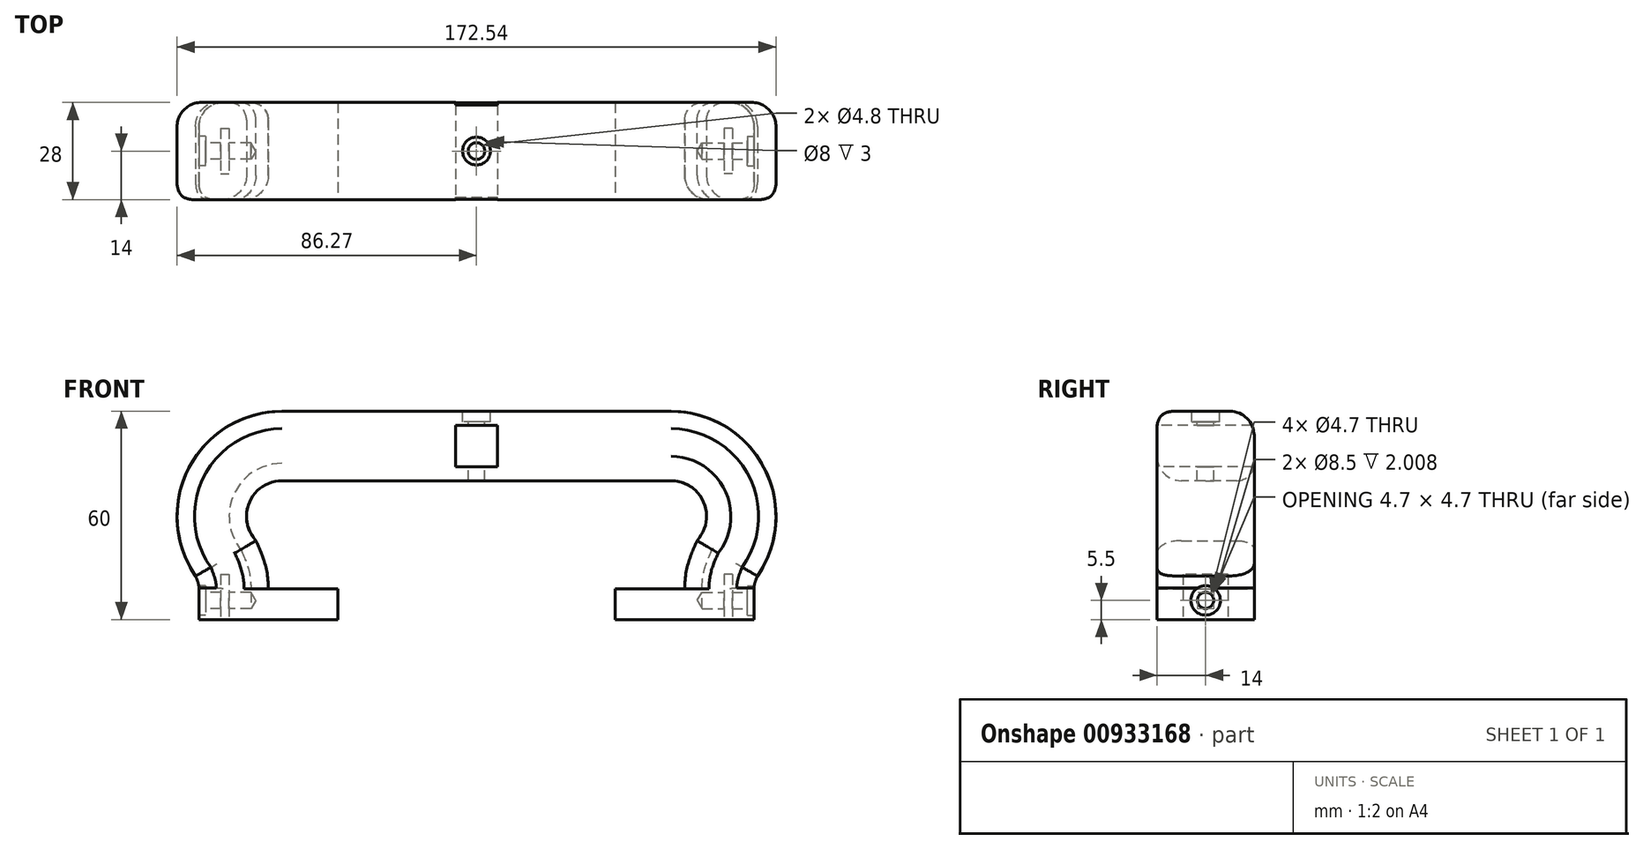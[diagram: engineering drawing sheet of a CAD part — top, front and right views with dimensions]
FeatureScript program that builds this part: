
annotation { "Feature Type Name" : "Feature", "Feature Type Description" : "" }
export const myFeature = defineFeature(function(context is Context, id is Id, definition is map)
    precondition{}
    {
        {
            var Q0;
            Q0=qCreatedBy(makeId("Right.planeOp"),FACE);
            var sketch = newSketch(context, id + "F0", { "sketchPlane" : qUnion([Q0])});
            skLineSegment(sketch, "E0.bottom", {"start": v(14, 60) * mm, "end": v(-14, 60) * mm});
            skLineSegment(sketch, "E0.top", {"start": v(14, 40) * mm, "end": v(-14, 40) * mm});
            skLineSegment(sketch, "E0.left", {"start": v(14, 40) * mm, "end": v(14, 60) * mm});
            skLineSegment(sketch, "E0.right", {"start": v(-14, 40) * mm, "end": v(-14, 60) * mm});
            skPoint(sketch, "E0.middle", {"position": v(0, 50) * mm});
            skSolve(sketch);
        }
        {
            var Q0;
            Q0=qCreatedBy(makeId("Front.planeOp"),FACE);
            var sketch = newSketch(context, id + "F1", { "sketchPlane" : qUnion([Q0])});
            skPoint(sketch, "E1.0", {"position": v(0, 50) * mm});
            skPoint(sketch, "E2", {"position": v(70, 0) * mm});
            skLineSegment(sketch, "E3", {"start": v(0, 50) * mm, "end": v(56.02, 50) * mm});
            skLineSegment(sketch, "E4", {"start": v(70, 0) * mm, "end": v(70, 8.96) * mm});
            skPoint(sketch, "E5", {"position": v(72.2, 17.57) * mm});
            skFitSpline(sketch, "E6", {"points": [v(72.2, 17.57) * mm, v(70, 8.96) * mm], "startDerivative": vector(-4.3, -9.4) * mm, "endDerivative": vector(0.3, -8.61) * mm});
            skArc(sketch, "E7", {"start": v(56.02, 50) * mm, "mid": v(74.14, 38.79) * mm, "end": v(72.2, 17.57) * mm});
            skSolve(sketch);
        }
        {
            var Q0;
            Q0=makeQuery(id+"F0.imprint","IMPRINT",FACE,{"disambiguationData":[TD([[makeQuery(id+"F0.imprint","IMPRINT",EDGE,{"derivedFrom":sQuery(id+"F0.wireOp",EDGE,"E0.bottom")}),1.0]])]});
            var Q1;
            Q1=sQuery(id+"F1.wireOp",EDGE,"E3");
            var Q2;
            Q2=sQuery(id+"F1.wireOp",EDGE,"E7");
            var Q3;
            Q3=sQuery(id+"F1.wireOp",EDGE,"E6");
            var Q4;
            Q4=sQuery(id+"F1.wireOp",EDGE,"E4");
            sweep(context, id + "F2", {"profiles" : qUnion([Q0]), "path" : qUnion([Q1, Q2, Q3, Q4])});
        }
        {
            var Q0;
            Q0=makeQuery(id+"F2.opSweep","SWEPT_BODY",BODY,{"disambiguationData":[OSD([sQuery(id+"F0.wireOp",EDGE,"E0.bottom"),sQuery(id+"F0.wireOp",EDGE,"E0.top"),sQuery(id+"F0.wireOp",EDGE,"E0.left"),sQuery(id+"F0.wireOp",EDGE,"E0.right"),sQuery(id+"F1.wireOp",EDGE,"E4")])]});
            var Q1;
            Q1=qCreatedBy(makeId("Right.planeOp"),FACE);
            mirror(context, id + "F3", {"operationType" : NewBodyOperationType.ADD, "entities" : qUnion([Q0]), "mirrorPlane" : qUnion([Q1])});
        }
        {
            var Q0;
            {var subQ0=makeQuery(id+"F2.opSweep","SWEPT_FACE",FACE,{"disambiguationData":[OSD([sQuery(id+"F0.wireOp",EDGE,"E0.right"),sQuery(id+"F1.wireOp",EDGE,"E3")])]});Q0=makeQuery(id+"F3.boolean.opBoolean","MERGE",FACE,{"derivedFrom":[subQ0,makeQuery(id+"F3.opPattern","COPY",FACE,{"derivedFrom":subQ0,"instanceName":"1"})]});}
            var sketch = newSketch(context, id + "F4", { "sketchPlane" : qUnion([Q0])});
            skLineSegment(sketch, "E8.0", {"start": v(0, 40) * mm, "end": v(0, 60) * mm});
            skPoint(sketch, "E9", {"position": v(0, 50) * mm});
            skLineSegment(sketch, "E10.bottom", {"start": v(6, 44) * mm, "end": v(-6, 44) * mm});
            skLineSegment(sketch, "E10.top", {"start": v(6, 56) * mm, "end": v(-6, 56) * mm});
            skLineSegment(sketch, "E10.left", {"start": v(6, 44) * mm, "end": v(6, 56) * mm});
            skLineSegment(sketch, "E10.right", {"start": v(-6, 44) * mm, "end": v(-6, 56) * mm});
            skSolve(sketch);
        }
        {
            var Q0;
            {var subQ5=sQuery(id+"F4.wireOp",EDGE,"E10.right");Q0=makeQuery(id+"F4.imprint","IMPRINT",FACE,{"disambiguationData":[TD([[makeQuery(id+"F4.imprint","IMPRINT",EDGE,{"derivedFrom":subQ5}),-1.0]])]});}
            var Q1;
            {var subQ5=sQuery(id+"F4.wireOp",EDGE,"E10.left");Q1=makeQuery(id+"F4.imprint","IMPRINT",FACE,{"disambiguationData":[TD([[makeQuery(id+"F4.imprint","IMPRINT",EDGE,{"derivedFrom":subQ5}),1.0]])]});}
            extrude(context, id + "F5", {"entities" : qUnion([Q0, Q1]), "operationType" : NewBodyOperationType.REMOVE, "endBound" : BoundingType.THROUGH_ALL, "oppositeDirection" : true, "depth" : 18 * mm, "offsetDistance" : 25 * mm});
        }
        {
            var Q0;
            Q0=makeQuery(id+"F2.opSweep","CAP_FACE",FACE,{"disambiguationData":[OSD([sQuery(id+"F0.wireOp",EDGE,"E0.bottom"),sQuery(id+"F0.wireOp",EDGE,"E0.top"),sQuery(id+"F0.wireOp",EDGE,"E0.left"),sQuery(id+"F0.wireOp",EDGE,"E0.right"),sQuery(id+"F1.wireOp",VERTEX,"E4.start")])],"isStart":false});
            var sketch = newSketch(context, id + "F6", { "sketchPlane" : qUnion([Q0])});
            skLineSegment(sketch, "E11.0", {"start": v(0, -14) * mm, "end": v(0, 14) * mm, "construction": true});
            skLineSegment(sketch, "E12", {"start": v(72.5, 14) * mm, "end": v(72.5, -14) * mm, "construction": true});
            skLineSegment(sketch, "E13.MirrorCS", {"start": v(-72.5, 14) * mm, "end": v(-72.5, -14) * mm, "construction": true});
            skPoint(sketch, "E14", {"position": v(72.5, 0) * mm});
            skLineSegment(sketch, "E15.bottom", {"start": v(73.7, -6.5) * mm, "end": v(71.3, -6.5) * mm});
            skLineSegment(sketch, "E15.top", {"start": v(73.7, 6.5) * mm, "end": v(71.3, 6.5) * mm});
            skLineSegment(sketch, "E15.left", {"start": v(73.7, -6.5) * mm, "end": v(73.7, 6.5) * mm});
            skLineSegment(sketch, "E15.right", {"start": v(71.3, -6.5) * mm, "end": v(71.3, 6.5) * mm});
            skLineSegment(sketch, "E16.MirrorCS", {"start": v(-71.3, -6.5) * mm, "end": v(-71.3, 6.5) * mm});
            skLineSegment(sketch, "E17.MirrorCS", {"start": v(-73.7, -6.5) * mm, "end": v(-73.7, 6.5) * mm});
            skLineSegment(sketch, "E18.MirrorCS", {"start": v(-73.7, 6.5) * mm, "end": v(-71.3, 6.5) * mm});
            skLineSegment(sketch, "E19.MirrorCS", {"start": v(-73.7, -6.5) * mm, "end": v(-71.3, -6.5) * mm});
            skSolve(sketch);
        }
        {
            var Q0;
            Q0=makeQuery(id+"F6.imprint","IMPRINT",FACE,{"disambiguationData":[TD([[makeQuery(id+"F6.imprint","IMPRINT",EDGE,{"derivedFrom":sQuery(id+"F6.wireOp",EDGE,"E15.bottom")}),-1.0]])]});
            var Q1;
            Q1=makeQuery(id+"F6.imprint","IMPRINT",FACE,{"disambiguationData":[TD([[makeQuery(id+"F6.imprint","IMPRINT",EDGE,{"derivedFrom":sQuery(id+"F6.wireOp",EDGE,"E16.MirrorCS")}),1.0]])]});
            extrude(context, id + "F7", {"entities" : qUnion([Q0, Q1]), "operationType" : NewBodyOperationType.REMOVE, "oppositeDirection" : true, "depth" : 13 * mm, "offsetDistance" : 25 * mm});
        }
        {
            var Q0;
            Q0=makeQuery(id+"F2.opSweep","SWEPT_FACE",FACE,{"disambiguationData":[OSD([sQuery(id+"F0.wireOp",EDGE,"E0.bottom"),sQuery(id+"F1.wireOp",EDGE,"E4")])]});
            var sketch = newSketch(context, id + "F8", { "sketchPlane" : qUnion([Q0])});
            skPoint(sketch, "E20", {"position": v(0, 5.5) * mm});
            skPoint(sketch, "E20.positionSnap0", {"position": v(0, 9.13) * mm});
            skSolve(sketch);
        }
        {
            var Q0;
            Q0=makeQuery(id+"F2.opSweep","SWEPT_FACE",FACE,{"disambiguationData":[OSD([sQuery(id+"F0.wireOp",EDGE,"E0.top"),sQuery(id+"F1.wireOp",EDGE,"E4")])]});
            extrude(context, id + "F9", {"entities" : qUnion([Q0]), "operationType" : NewBodyOperationType.ADD, "depth" : 20 * mm, "offsetDistance" : 25 * mm});
        }
        {
            var Q0;
            Q0=makeQuery(id+"F3.opPattern","COPY",FACE,{"derivedFrom":makeQuery(id+"F2.opSweep","SWEPT_FACE",FACE,{"disambiguationData":[OSD([sQuery(id+"F0.wireOp",EDGE,"E0.bottom"),sQuery(id+"F1.wireOp",EDGE,"E4")])]}),"instanceName":"1"});
            var sketch = newSketch(context, id + "F10", { "sketchPlane" : qUnion([Q0])});
            skPoint(sketch, "E21", {"position": v(0, 5.5) * mm});
            skPoint(sketch, "E21.positionSnap0", {"position": v(0, 9.13) * mm});
            skSolve(sketch);
        }
        {
            var Q0;
            Q0=makeQuery(id+"F3.opPattern","COPY",FACE,{"derivedFrom":makeQuery(id+"F2.opSweep","SWEPT_FACE",FACE,{"disambiguationData":[OSD([sQuery(id+"F0.wireOp",EDGE,"E0.top"),sQuery(id+"F1.wireOp",EDGE,"E4")])]}),"instanceName":"1"});
            extrude(context, id + "F11", {"entities" : qUnion([Q0]), "operationType" : NewBodyOperationType.ADD, "depth" : 20 * mm, "offsetDistance" : 25 * mm});
        }
        {
            var Q0;
            {var subQ0=makeQuery(id+"F2.opSweep","SWEPT_FACE",FACE,{"disambiguationData":[OSD([sQuery(id+"F0.wireOp",EDGE,"E0.bottom"),sQuery(id+"F1.wireOp",EDGE,"E3")])]});Q0=makeQuery(id+"F3.boolean.opBoolean","MERGE",FACE,{"derivedFrom":[subQ0,makeQuery(id+"F3.opPattern","COPY",FACE,{"derivedFrom":subQ0,"instanceName":"1"})]});}
            var sketch = newSketch(context, id + "F12", { "sketchPlane" : qUnion([Q0])});
            skPoint(sketch, "E22", {"position": v(0, 0) * mm});
            skSolve(sketch);
        }
        {
            var Q0;
            Q0=sQuery(id+"F12.wireOp",VERTEX,"E22");
            var Q1;
            Q1=makeQuery(id+"F2.opSweep","SWEPT_BODY",BODY,{"disambiguationData":[OSD([sQuery(id+"F0.wireOp",EDGE,"E0.bottom"),sQuery(id+"F0.wireOp",EDGE,"E0.top"),sQuery(id+"F0.wireOp",EDGE,"E0.left"),sQuery(id+"F0.wireOp",EDGE,"E0.right"),sQuery(id+"F1.wireOp",EDGE,"E4")])]});
            hole(context, id + "F13", {"style" : HoleStyle.C_BORE, "endStyle" : HoleEndStyle.THROUGH, "holeDiameter" : 4.8 * mm, "cBoreDiameter" : 8 * mm, "cBoreDepth" : 3 * mm, "majorDiameter" : 5 * mm, "isTappedThrough" : true, "tappedDepth" : 12 * mm, "tapClearance" : 3, "locations" : qUnion([Q0]), "scope" : qUnion([Q1])});
        }
        {
            var Q0;
            {var subQ0=makeQuery(id+"F2.opSweep","SWEPT_EDGE",EDGE,{"disambiguationData":[OSD([sQuery(id+"F0.wireOp",EDGE,"E0.bottom"),sQuery(id+"F0.wireOp",EDGE,"E0.right"),sQuery(id+"F1.wireOp",EDGE,"E3")])]});Q0=makeQuery(id+"F3.boolean.opBoolean","MERGE",EDGE,{"derivedFrom":[subQ0,makeQuery(id+"F3.opPattern","COPY",EDGE,{"derivedFrom":subQ0,"instanceName":"1"})]});}
            var Q1;
            Q1=makeQuery(id+"F2.opSweep","SWEPT_EDGE",EDGE,{"disambiguationData":[OSD([sQuery(id+"F0.wireOp",EDGE,"E0.bottom"),sQuery(id+"F0.wireOp",EDGE,"E0.right"),sQuery(id+"F1.wireOp",EDGE,"E7")])]});
            var Q2;
            Q2=makeQuery(id+"F2.opSweep","SWEPT_EDGE",EDGE,{"disambiguationData":[OSD([sQuery(id+"F0.wireOp",EDGE,"E0.bottom"),sQuery(id+"F0.wireOp",EDGE,"E0.right"),sQuery(id+"F1.wireOp",EDGE,"E6")]),OD(1.0)]});
            var Q3;
            {var subQ0=sQuery(id+"F19.hole-0.sketch.wireOp",EDGE,"cbore_start_line_2");Q3=makeQuery(id+"F19.hole-0.boolean.opBoolean","COPY",EDGE,{"disambiguationData":[topologyDisambiguationEdgeConnected([makeQuery(id+"F2.opSweep","SWEPT_FACE",FACE,{"disambiguationData":[OSD([sQuery(id+"F0.wireOp",EDGE,"E0.bottom"),sQuery(id+"F1.wireOp",EDGE,"E4")])]}),makeQuery(id+"F19.hole-0.opRevolve","SWEPT_FACE",FACE,{"disambiguationData":[OSD([subQ0])]})])],"derivedFrom":makeQuery(id+"F19.hole-0.opRevolve","SWEPT_EDGE",EDGE,{"disambiguationData":[OSD([subQ0,sQuery(id+"F19.hole-0.sketch.wireOp",EDGE,"cbore_start_line_3")])]})});}
            var Q4;
            Q4=makeQuery(id+"F2.opSweep","SWEPT_EDGE",EDGE,{"disambiguationData":[OSD([sQuery(id+"F0.wireOp",EDGE,"E0.bottom"),sQuery(id+"F0.wireOp",EDGE,"E0.right"),sQuery(id+"F1.wireOp",EDGE,"E4")])]});
            var Q5;
            Q5=makeQuery(id+"F3.opPattern","COPY",EDGE,{"derivedFrom":makeQuery(id+"F2.opSweep","SWEPT_EDGE",EDGE,{"disambiguationData":[OSD([sQuery(id+"F0.wireOp",EDGE,"E0.bottom"),sQuery(id+"F0.wireOp",EDGE,"E0.right"),sQuery(id+"F1.wireOp",EDGE,"E7")])]}),"instanceName":"1"});
            var Q6;
            Q6=makeQuery(id+"F3.opPattern","COPY",EDGE,{"derivedFrom":makeQuery(id+"F2.opSweep","SWEPT_EDGE",EDGE,{"disambiguationData":[OSD([sQuery(id+"F0.wireOp",EDGE,"E0.bottom"),sQuery(id+"F0.wireOp",EDGE,"E0.right"),sQuery(id+"F1.wireOp",EDGE,"E6")]),OD(1.0)]}),"instanceName":"1"});
            var Q7;
            Q7=makeQuery(id+"F3.opPattern","COPY",EDGE,{"derivedFrom":makeQuery(id+"F2.opSweep","SWEPT_EDGE",EDGE,{"disambiguationData":[OSD([sQuery(id+"F0.wireOp",EDGE,"E0.bottom"),sQuery(id+"F0.wireOp",EDGE,"E0.right"),sQuery(id+"F1.wireOp",EDGE,"E4")])]}),"instanceName":"1"});
            var Q8;
            Q8=makeQuery(id+"F2.opSweep","SWEPT_EDGE",EDGE,{"disambiguationData":[OSD([sQuery(id+"F0.wireOp",EDGE,"E0.bottom"),sQuery(id+"F0.wireOp",EDGE,"E0.right"),sQuery(id+"F1.wireOp",EDGE,"E6")]),OD(0.0)]});
            var Q9;
            Q9=makeQuery(id+"F3.opPattern","COPY",EDGE,{"derivedFrom":makeQuery(id+"F2.opSweep","SWEPT_EDGE",EDGE,{"disambiguationData":[OSD([sQuery(id+"F0.wireOp",EDGE,"E0.bottom"),sQuery(id+"F0.wireOp",EDGE,"E0.right"),sQuery(id+"F1.wireOp",EDGE,"E6")]),OD(0.0)]}),"instanceName":"1"});
            fillet(context, id + "F14", {"entities" : qUnion([Q0, Q1, Q2, Q3, Q4, Q5, Q6, Q7, Q8, Q9]), "radius" : 5 * mm, "tangentPropagation" : true, "rho" : 0.5, "crossSection" : FilletCrossSection.CONIC, "allowEdgeOverflow" : false});
        }
        {
            var Q0;
            Q0=makeQuery(id+"F3.opPattern","COPY",EDGE,{"derivedFrom":makeQuery(id+"F2.opSweep","SWEPT_EDGE",EDGE,{"disambiguationData":[OSD([sQuery(id+"F0.wireOp",EDGE,"E0.top"),sQuery(id+"F0.wireOp",EDGE,"E0.right"),sQuery(id+"F1.wireOp",EDGE,"E6")]),OD(0.0)]}),"instanceName":"1"});
            var Q1;
            Q1=makeQuery(id+"F2.opSweep","SWEPT_EDGE",EDGE,{"disambiguationData":[OSD([sQuery(id+"F0.wireOp",EDGE,"E0.top"),sQuery(id+"F0.wireOp",EDGE,"E0.right"),sQuery(id+"F1.wireOp",EDGE,"E6")]),OD(0.0)]});
            var Q2;
            Q2=makeQuery(id+"F2.opSweep","SWEPT_EDGE",EDGE,{"disambiguationData":[OSD([sQuery(id+"F0.wireOp",EDGE,"E0.top"),sQuery(id+"F0.wireOp",EDGE,"E0.right"),sQuery(id+"F1.wireOp",EDGE,"E7")]),OD(0.0)]});
            fillet(context, id + "F15", {"entities" : qUnion([Q0, Q1, Q2]), "radius" : 7 * mm, "tangentPropagation" : true, "allowEdgeOverflow" : false});
        }
        {
            var Q0;
            Q0=makeQuery(id+"F2.opSweep","SWEPT_EDGE",EDGE,{"disambiguationData":[OSD([sQuery(id+"F0.wireOp",EDGE,"E0.bottom"),sQuery(id+"F0.wireOp",EDGE,"E0.left"),sQuery(id+"F1.wireOp",EDGE,"E4")])]});
            var Q1;
            Q1=makeQuery(id+"F2.opSweep","SWEPT_EDGE",EDGE,{"disambiguationData":[OSD([sQuery(id+"F0.wireOp",EDGE,"E0.bottom"),sQuery(id+"F0.wireOp",EDGE,"E0.left"),sQuery(id+"F1.wireOp",EDGE,"E7")])]});
            var Q2;
            {var subQ0=makeQuery(id+"F2.opSweep","SWEPT_EDGE",EDGE,{"disambiguationData":[OSD([sQuery(id+"F0.wireOp",EDGE,"E0.bottom"),sQuery(id+"F0.wireOp",EDGE,"E0.left"),sQuery(id+"F1.wireOp",EDGE,"E3")])]});Q2=makeQuery(id+"F3.boolean.opBoolean","MERGE",EDGE,{"derivedFrom":[subQ0,makeQuery(id+"F3.opPattern","COPY",EDGE,{"derivedFrom":subQ0,"instanceName":"1"})]});}
            var Q3;
            Q3=makeQuery(id+"F3.opPattern","COPY",EDGE,{"derivedFrom":makeQuery(id+"F2.opSweep","SWEPT_EDGE",EDGE,{"disambiguationData":[OSD([sQuery(id+"F0.wireOp",EDGE,"E0.bottom"),sQuery(id+"F0.wireOp",EDGE,"E0.left"),sQuery(id+"F1.wireOp",EDGE,"E4")])]}),"instanceName":"1"});
            var Q4;
            Q4=makeQuery(id+"F3.opPattern","COPY",EDGE,{"derivedFrom":makeQuery(id+"F2.opSweep","SWEPT_EDGE",EDGE,{"disambiguationData":[OSD([sQuery(id+"F0.wireOp",EDGE,"E0.bottom"),sQuery(id+"F0.wireOp",EDGE,"E0.left"),sQuery(id+"F1.wireOp",EDGE,"E6")]),OD(1.0)]}),"instanceName":"1"});
            var Q5;
            Q5=makeQuery(id+"F3.opPattern","COPY",EDGE,{"derivedFrom":makeQuery(id+"F2.opSweep","SWEPT_EDGE",EDGE,{"disambiguationData":[OSD([sQuery(id+"F0.wireOp",EDGE,"E0.bottom"),sQuery(id+"F0.wireOp",EDGE,"E0.left"),sQuery(id+"F1.wireOp",EDGE,"E7")])]}),"instanceName":"1"});
            var Q6;
            Q6=makeQuery(id+"F2.opSweep","SWEPT_EDGE",EDGE,{"disambiguationData":[OSD([sQuery(id+"F0.wireOp",EDGE,"E0.bottom"),sQuery(id+"F0.wireOp",EDGE,"E0.left"),sQuery(id+"F1.wireOp",EDGE,"E6")]),OD(1.0)]});
            fillet(context, id + "F16", {"entities" : qUnion([Q0, Q1, Q2, Q3, Q4, Q5, Q6]), "radius" : 7 * mm, "tangentPropagation" : true, "allowEdgeOverflow" : false});
        }
        {
            var Q0;
            Q0=makeQuery(id+"F2.opSweep","SWEPT_EDGE",EDGE,{"disambiguationData":[OSD([sQuery(id+"F0.wireOp",EDGE,"E0.top"),sQuery(id+"F0.wireOp",EDGE,"E0.left"),sQuery(id+"F1.wireOp",EDGE,"E6")]),OD(0.0)]});
            var Q1;
            Q1=makeQuery(id+"F3.opPattern","COPY",EDGE,{"derivedFrom":makeQuery(id+"F2.opSweep","SWEPT_EDGE",EDGE,{"disambiguationData":[OSD([sQuery(id+"F0.wireOp",EDGE,"E0.top"),sQuery(id+"F0.wireOp",EDGE,"E0.left"),sQuery(id+"F1.wireOp",EDGE,"E6")]),OD(0.0)]}),"instanceName":"1"});
            var Q2;
            Q2=makeQuery(id+"F3.opPattern","COPY",EDGE,{"derivedFrom":makeQuery(id+"F2.opSweep","SWEPT_EDGE",EDGE,{"disambiguationData":[OSD([sQuery(id+"F0.wireOp",EDGE,"E0.top"),sQuery(id+"F0.wireOp",EDGE,"E0.left"),sQuery(id+"F1.wireOp",EDGE,"E7")]),OD(0.0)]}),"instanceName":"1"});
            var Q3;
            {var subQ0=makeQuery(id+"F2.opSweep","SWEPT_EDGE",EDGE,{"disambiguationData":[OSD([sQuery(id+"F0.wireOp",EDGE,"E0.top"),sQuery(id+"F0.wireOp",EDGE,"E0.left"),sQuery(id+"F1.wireOp",EDGE,"E3")])]});Q3=makeQuery(id+"F3.boolean.opBoolean","MERGE",EDGE,{"derivedFrom":[subQ0,makeQuery(id+"F3.opPattern","COPY",EDGE,{"derivedFrom":subQ0,"instanceName":"1"})]});}
            var Q4;
            Q4=makeQuery(id+"F2.opSweep","SWEPT_EDGE",EDGE,{"disambiguationData":[OSD([sQuery(id+"F0.wireOp",EDGE,"E0.top"),sQuery(id+"F0.wireOp",EDGE,"E0.left"),sQuery(id+"F1.wireOp",EDGE,"E7")]),OD(0.0)]});
            fillet(context, id + "F17", {"entities" : qUnion([Q0, Q1, Q2, Q3, Q4]), "radius" : 5 * mm, "tangentPropagation" : true, "allowEdgeOverflow" : false});
        }
        {
            var Q0;
            Q0=sQuery(id+"F10.wireOp",VERTEX,"E21");
            var Q1;
            Q1=makeQuery(id+"F2.opSweep","SWEPT_BODY",BODY,{"disambiguationData":[OSD([sQuery(id+"F0.wireOp",EDGE,"E0.bottom"),sQuery(id+"F0.wireOp",EDGE,"E0.top"),sQuery(id+"F0.wireOp",EDGE,"E0.left"),sQuery(id+"F0.wireOp",EDGE,"E0.right"),sQuery(id+"F1.wireOp",EDGE,"E4")])]});
            hole(context, id + "F18", {"style" : HoleStyle.C_BORE, "endStyle" : HoleEndStyle.BLIND, "holeDiameter" : 4.7 * mm, "cBoreDiameter" : 8.5 * mm, "cBoreDepth" : 2 * mm, "majorDiameter" : 5 * mm, "holeDepth" : 15 * mm, "isTappedThrough" : true, "tappedDepth" : 12 * mm, "tapClearance" : 3, "locations" : qUnion([Q0]), "scope" : qUnion([Q1])});
        }
        {
            var Q0;
            Q0=sQuery(id+"F8.wireOp",VERTEX,"E20");
            var Q1;
            Q1=makeQuery(id+"F2.opSweep","SWEPT_BODY",BODY,{"disambiguationData":[OSD([sQuery(id+"F0.wireOp",EDGE,"E0.bottom"),sQuery(id+"F0.wireOp",EDGE,"E0.top"),sQuery(id+"F0.wireOp",EDGE,"E0.left"),sQuery(id+"F0.wireOp",EDGE,"E0.right"),sQuery(id+"F1.wireOp",EDGE,"E4")])]});
            hole(context, id + "F19", {"style" : HoleStyle.C_BORE, "endStyle" : HoleEndStyle.BLIND, "holeDiameter" : 4.7 * mm, "cBoreDiameter" : 8.5 * mm, "cBoreDepth" : 2 * mm, "majorDiameter" : 5 * mm, "holeDepth" : 15 * mm, "isTappedThrough" : true, "tappedDepth" : 12 * mm, "tapClearance" : 3, "locations" : qUnion([Q0]), "scope" : qUnion([Q1])});
        }
    });
